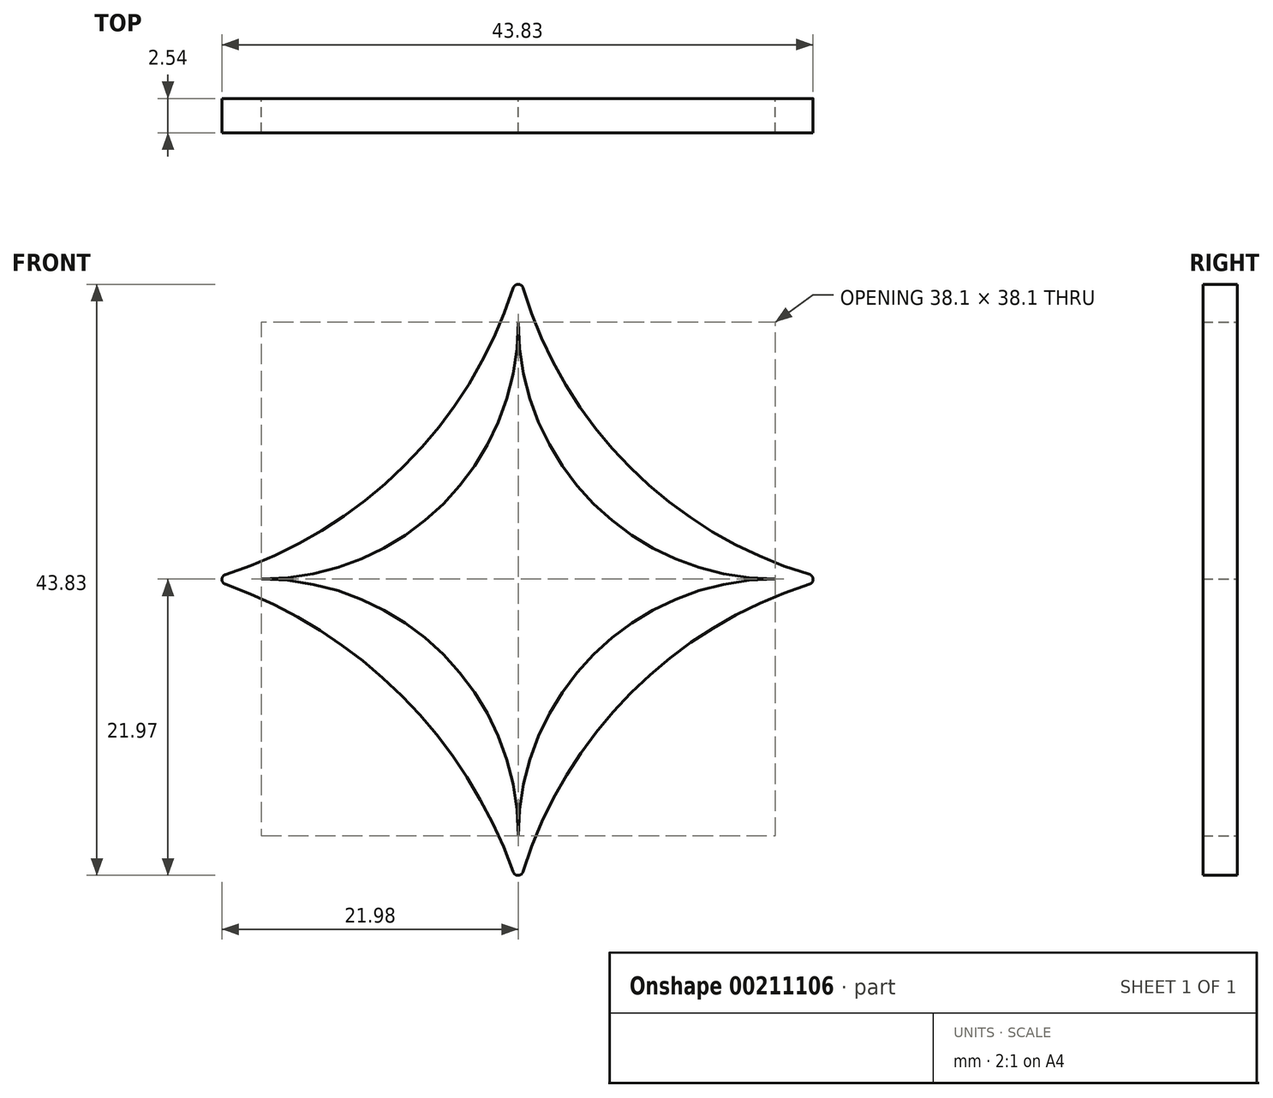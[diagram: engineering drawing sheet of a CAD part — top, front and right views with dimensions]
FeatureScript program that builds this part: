
annotation { "Feature Type Name" : "Feature", "Feature Type Description" : "" }
export const myFeature = defineFeature(function(context is Context, id is Id, definition is map)
    precondition{}
    {
        {
            var Q0;
            Q0=qCreatedBy(makeId("Front.planeOp"),FACE);
            var sketch = newSketch(context, id + "F0", { "sketchPlane" : qUnion([Q0])});
            skLineSegment(sketch, "E0", {"start": v(0, 0) * mm, "end": v(0, -19.05) * mm});
            skLineSegment(sketch, "E1", {"start": v(0, -19.05) * mm, "end": v(0, 0) * mm});
            skLineSegment(sketch, "E2", {"start": v(0, 0) * mm, "end": v(0, 19.05) * mm});
            skLineSegment(sketch, "E3", {"start": v(0, 0) * mm, "end": v(19.05, 0) * mm});
            skLineSegment(sketch, "E4", {"start": v(0, 0) * mm, "end": v(-19.05, 0) * mm});
            skArc(sketch, "E5", {"start": v(-19.05, 0) * mm, "mid": v(-5.58, 5.58) * mm, "end": v(0, 19.05) * mm});
            skArc(sketch, "E6", {"start": v(0, 19.05) * mm, "mid": v(5.58, 5.58) * mm, "end": v(19.05, 0) * mm});
            skArc(sketch, "E7", {"start": v(19.05, 0) * mm, "mid": v(5.58, -5.58) * mm, "end": v(0, -19.05) * mm});
            skArc(sketch, "E8", {"start": v(0, -19.05) * mm, "mid": v(-5.58, -5.58) * mm, "end": v(-19.05, 0) * mm});
            skLineSegment(sketch, "E9.0", {"start": v(22.86, -19.05) * mm, "end": v(22.86, 0) * mm});
            skLineSegment(sketch, "E10.0", {"start": v(0, -22.86) * mm, "end": v(19.05, -22.86) * mm});
            skLineSegment(sketch, "E11.0", {"start": v(0, 22.86) * mm, "end": v(-19.05, 22.86) * mm});
            skLineSegment(sketch, "E12.0", {"start": v(-22.86, -19.05) * mm, "end": v(-22.86, 0) * mm});
            skArc(sketch, "E13", {"start": v(-22.86, 0) * mm, "mid": v(-8.43, 8.43) * mm, "end": v(0, 22.86) * mm});
            skArc(sketch, "E14", {"start": v(0, 22.86) * mm, "mid": v(8.28, 8.28) * mm, "end": v(22.86, 0) * mm});
            skArc(sketch, "E15", {"start": v(22.86, 0) * mm, "mid": v(8.4, -8.4) * mm, "end": v(0, -22.86) * mm});
            skArc(sketch, "E16", {"start": v(0, -22.86) * mm, "mid": v(-8.65, -8.65) * mm, "end": v(-22.86, 0) * mm});
            skLineSegment(sketch, "E17.0", {"start": v(1.27, 0) * mm, "end": v(1.27, 19.05) * mm});
            skLineSegment(sketch, "E18.0", {"start": v(1.27, -19.05) * mm, "end": v(1.27, 0) * mm});
            skLineSegment(sketch, "E19.0", {"start": v(-1.27, -19.05) * mm, "end": v(-1.27, 0) * mm});
            skLineSegment(sketch, "E20.0", {"start": v(-1.27, 0) * mm, "end": v(-1.27, 19.05) * mm});
            skSolve(sketch);
        }
        {
            var Q0;
            Q0=makeQuery(id+"F0.imprint","IMPRINT",FACE,{"disambiguationData":[TD([[makeQuery(id+"F0.imprint","IMPRINT",EDGE,{"derivedFrom":sQuery(id+"F0.wireOp",EDGE,"E5")}),1.0]])]});
            extrude(context, id + "F2", {"entities" : qUnion([Q0]), "depth" : 2.54 * mm});
        }
        {
            var Q0;
            Q0=makeQuery(id+"F2.opExtrude","SWEPT_EDGE",EDGE,{"disambiguationData":[OSD([sQuery(id+"F0.wireOp",EDGE,"E13"),sQuery(id+"F0.wireOp",EDGE,"E14")])]});
            var Q1;
            Q1=makeQuery(id+"F2.opExtrude","SWEPT_EDGE",EDGE,{"disambiguationData":[OSD([sQuery(id+"F0.wireOp",EDGE,"E14"),sQuery(id+"F0.wireOp",EDGE,"E15")])]});
            var Q2;
            Q2=makeQuery(id+"F2.opExtrude","SWEPT_EDGE",EDGE,{"disambiguationData":[OSD([sQuery(id+"F0.wireOp",EDGE,"E15"),sQuery(id+"F0.wireOp",EDGE,"E16")])]});
            var Q3;
            Q3=makeQuery(id+"F2.opExtrude","SWEPT_EDGE",EDGE,{"disambiguationData":[OSD([sQuery(id+"F0.wireOp",EDGE,"E13"),sQuery(id+"F0.wireOp",EDGE,"E16")])]});
            fillet(context, id + "F1", {"entities" : qUnion([Q0, Q1, Q2, Q3]), "radius" : 0.38 * mm, "tangentPropagation" : true, "allowEdgeOverflow" : false});
        }
    });
